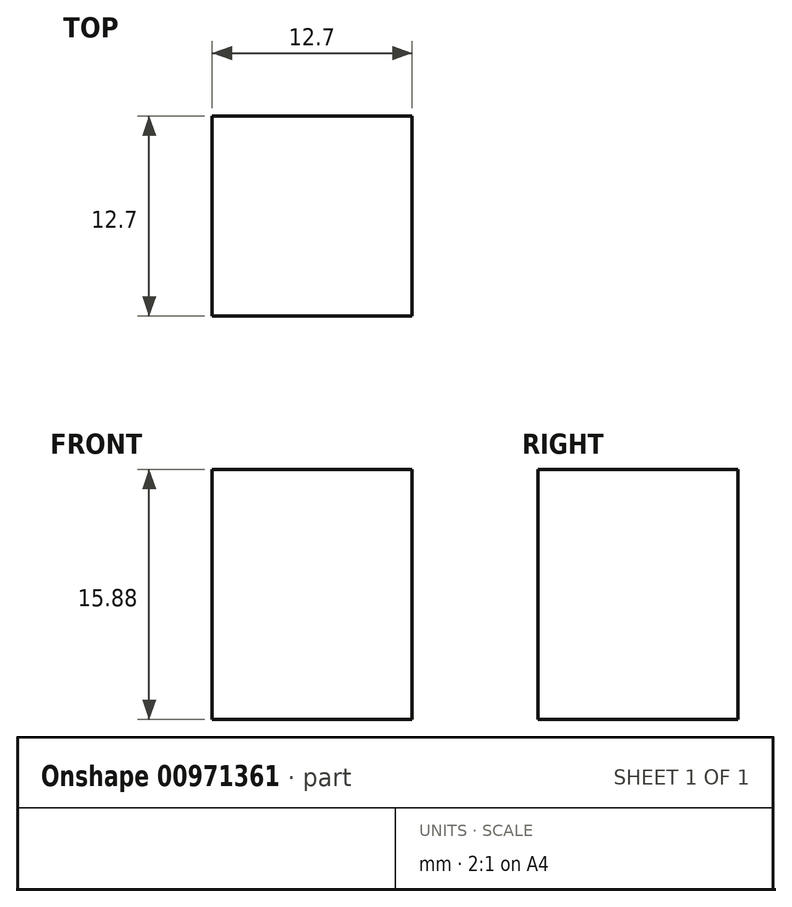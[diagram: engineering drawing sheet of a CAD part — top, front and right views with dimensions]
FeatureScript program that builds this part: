
annotation { "Feature Type Name" : "Feature", "Feature Type Description" : "" }
export const myFeature = defineFeature(function(context is Context, id is Id, definition is map)
    precondition{}
    {
        {
            var Q0;
            Q0=qCreatedBy(makeId("Top.planeOp"),FACE);
            var sketch = newSketch(context, id + "F0", { "sketchPlane" : qUnion([Q0])});
            skLineSegment(sketch, "E0.bottom", {"start": v(6.35, 6.35) * mm, "end": v(-6.35, 6.35) * mm});
            skLineSegment(sketch, "E0.top", {"start": v(6.35, -6.35) * mm, "end": v(-6.35, -6.35) * mm});
            skLineSegment(sketch, "E0.left", {"start": v(6.35, 6.35) * mm, "end": v(6.35, -6.35) * mm});
            skLineSegment(sketch, "E0.right", {"start": v(-6.35, 6.35) * mm, "end": v(-6.35, -6.35) * mm});
            skPoint(sketch, "E0.middle", {"position": v(0, 0) * mm});
            skSolve(sketch);
        }
        {
            var Q0;
            Q0=makeQuery(id+"F0.imprint","IMPRINT",FACE,{"disambiguationData":[TD([[makeQuery(id+"F0.imprint","IMPRINT",EDGE,{"derivedFrom":sQuery(id+"F0.wireOp",EDGE,"E0.bottom")}),1.0]])]});
            extrude(context, id + "F1", {"entities" : qUnion([Q0]), "depth" : 15.88 * mm, "offsetDistance" : 25.4 * mm});
        }
    });
